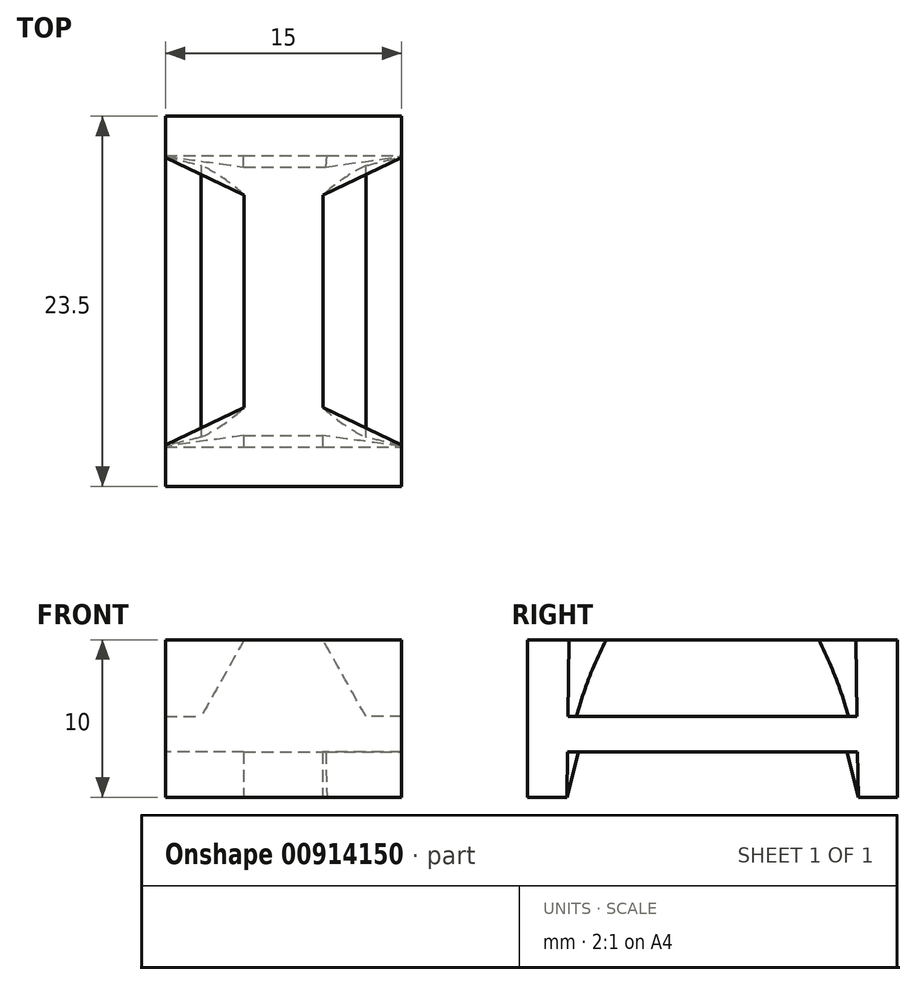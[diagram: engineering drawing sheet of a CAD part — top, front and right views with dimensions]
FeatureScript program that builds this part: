
annotation { "Feature Type Name" : "Feature", "Feature Type Description" : "" }
export const myFeature = defineFeature(function(context is Context, id is Id, definition is map)
    precondition{}
    {
        {
            var Q0;
            Q0=qCreatedBy(makeId("Top.planeOp"),FACE);
            var sketch = newSketch(context, id + "F0", { "sketchPlane" : qUnion([Q0])});
            skLineSegment(sketch, "E0.bottom", {"start": v(-7.5, 11.75) * mm, "end": v(7.5, 11.75) * mm});
            skLineSegment(sketch, "E0.top", {"start": v(-7.5, -11.75) * mm, "end": v(7.5, -11.75) * mm});
            skLineSegment(sketch, "E0.left", {"start": v(-7.5, 11.75) * mm, "end": v(-7.5, -11.75) * mm});
            skLineSegment(sketch, "E0.right", {"start": v(7.5, 11.75) * mm, "end": v(7.5, -11.75) * mm});
            skSolve(sketch);
        }
        {
            var Q0;
            Q0=makeQuery(id+"F0.imprint","IMPRINT",FACE,{"disambiguationData":[TD([[makeQuery(id+"F0.imprint","IMPRINT",EDGE,{"derivedFrom":sQuery(id+"F0.wireOp",EDGE,"E0.bottom")}),-1.0]])]});
            extrude(context, id + "F1", {"entities" : qUnion([Q0]), "depth" : 2.25 * mm, "offsetDistance" : 25 * mm, "symmetric" : true});
        }
        {
            var Q0;
            Q0=qCreatedBy(makeId("Top.planeOp"),FACE);
            cPlane(context, id + "F2", {"entities" : qUnion([Q0]), "cplaneType" : CPlaneType.OFFSET, "offset" : 6 * mm, "width" : 150 * mm, "height" : 150 * mm});
        }
        {
            var Q0;
            Q0=qCreatedBy(makeId("Top.planeOp"),FACE);
            cPlane(context, id + "F3", {"entities" : qUnion([Q0]), "cplaneType" : CPlaneType.OFFSET, "offset" : 4 * mm, "oppositeDirection" : true, "width" : 150 * mm, "height" : 150 * mm});
        }
        {
            var Q0;
            Q0=qCreatedBy(id+"F2.planeOp",FACE);
            var sketch = newSketch(context, id + "F4", { "sketchPlane" : qUnion([Q0])});
            skLineSegment(sketch, "E1", {"start": v(7.5, -11.75) * mm, "end": v(7.5, -9.12) * mm});
            skLineSegment(sketch, "E2", {"start": v(7.5, -9.12) * mm, "end": v(2.5, -6.75) * mm});
            skLineSegment(sketch, "E3", {"start": v(2.5, -6.75) * mm, "end": v(-2.5, -6.75) * mm});
            skLineSegment(sketch, "E4", {"start": v(-2.5, -6.75) * mm, "end": v(-7.5, -9.12) * mm});
            skLineSegment(sketch, "E5", {"start": v(-7.5, -9.12) * mm, "end": v(-7.5, -11.75) * mm});
            skLineSegment(sketch, "E6", {"start": v(-7.5, -11.75) * mm, "end": v(7.5, -11.75) * mm});
            skLineSegment(sketch, "E7.MirrorCS", {"start": v(-2.5, 6.75) * mm, "end": v(-7.5, 9.12) * mm});
            skLineSegment(sketch, "E8.MirrorCS", {"start": v(7.5, 11.75) * mm, "end": v(7.5, 9.12) * mm});
            skLineSegment(sketch, "E9.MirrorCS", {"start": v(7.5, 9.12) * mm, "end": v(2.5, 6.75) * mm});
            skLineSegment(sketch, "E10.MirrorCS", {"start": v(-7.5, 9.12) * mm, "end": v(-7.5, 11.75) * mm});
            skLineSegment(sketch, "E11.MirrorCS", {"start": v(2.5, 6.75) * mm, "end": v(-2.5, 6.75) * mm});
            skLineSegment(sketch, "E12.MirrorCS", {"start": v(-7.5, 11.75) * mm, "end": v(7.5, 11.75) * mm});
            skSolve(sketch);
        }
        {
            var Q0;
            Q0=qCreatedBy(id+"F3.planeOp",FACE);
            var sketch = newSketch(context, id + "F5", { "sketchPlane" : qUnion([Q0])});
            skLineSegment(sketch, "E13.bottom", {"start": v(-7.5, -11.75) * mm, "end": v(7.5, -11.75) * mm});
            skLineSegment(sketch, "E13.top", {"start": v(-7.5, -9.25) * mm, "end": v(-2.54, -9.25) * mm});
            skLineSegment(sketch, "E13.left", {"start": v(-7.5, -11.75) * mm, "end": v(-7.5, -9.25) * mm});
            skLineSegment(sketch, "E13.right", {"start": v(7.5, -11.75) * mm, "end": v(7.5, -9.25) * mm});
            skLineSegment(sketch, "E14.MirrorCS", {"start": v(7.5, 11.75) * mm, "end": v(7.5, 9.25) * mm});
            skLineSegment(sketch, "E15.MirrorCS", {"start": v(-7.5, 11.75) * mm, "end": v(-7.5, 9.25) * mm});
            skLineSegment(sketch, "E16.MirrorCS", {"start": v(-7.5, 9.25) * mm, "end": v(-2.54, 9.25) * mm});
            skLineSegment(sketch, "E17.MirrorCS", {"start": v(-7.5, 11.75) * mm, "end": v(7.5, 11.75) * mm});
            skLineSegment(sketch, "E18", {"start": v(-2.54, -9.25) * mm, "end": v(2.48, -9.25) * mm});
            skLineSegment(sketch, "E19", {"start": v(2.48, -9.25) * mm, "end": v(7.5, -9.25) * mm});
            skLineSegment(sketch, "E20", {"start": v(-2.54, 9.25) * mm, "end": v(2.76, 9.25) * mm});
            skLineSegment(sketch, "E21", {"start": v(2.76, 9.25) * mm, "end": v(7.5, 9.25) * mm});
            skSolve(sketch);
        }
        {
            var Q1;
            Q1=makeQuery(id+"F4.imprint","IMPRINT",FACE,{"disambiguationData":[TD([[makeQuery(id+"F4.imprint","IMPRINT",EDGE,{"derivedFrom":sQuery(id+"F4.wireOp",EDGE,"E7.MirrorCS")}),-1.0]])]});
            var Q2;
            Q2=makeQuery(id+"F5.imprint","IMPRINT",FACE,{"disambiguationData":[TD([[makeQuery(id+"F5.imprint","IMPRINT",EDGE,{"derivedFrom":sQuery(id+"F5.wireOp",EDGE,"E14.MirrorCS")}),-1.0]])]});
            loft(context, id + "F6", {"operationType" : NewBodyOperationType.ADD, "sheetProfilesArray" : [{ "sheetProfileEntities" : qUnion([Q1]) }, { "sheetProfileEntities" : qUnion([Q2]) }]});
        }
        {
            var Q1;
            Q1=makeQuery(id+"F4.imprint","IMPRINT",FACE,{"disambiguationData":[TD([[makeQuery(id+"F4.imprint","IMPRINT",EDGE,{"derivedFrom":sQuery(id+"F4.wireOp",EDGE,"E1")}),1.0]])]});
            var Q2;
            Q2=makeQuery(id+"F5.imprint","IMPRINT",FACE,{"disambiguationData":[TD([[makeQuery(id+"F5.imprint","IMPRINT",EDGE,{"derivedFrom":sQuery(id+"F5.wireOp",EDGE,"E13.bottom")}),1.0]])]});
            loft(context, id + "F7", {"operationType" : NewBodyOperationType.ADD, "sheetProfilesArray" : [{ "sheetProfileEntities" : qUnion([Q1]) }, { "sheetProfileEntities" : qUnion([Q2]) }]});
        }
        {
            var Q0;
            Q0=qCreatedBy(makeId("Front.planeOp"),FACE);
            cPlane(context, id + "F8", {"entities" : qUnion([Q0]), "cplaneType" : CPlaneType.OFFSET, "offset" : 10.1 * mm, "width" : 150 * mm, "height" : 150 * mm});
        }
        {
            var Q0;
            Q0=qCreatedBy(id+"F8.planeOp",FACE);
            var sketch = newSketch(context, id + "F9", { "sketchPlane" : qUnion([Q0])});
            skLineSegment(sketch, "E22", {"start": v(5.86, 0) * mm, "end": v(2.5, 6) * mm});
            skLineSegment(sketch, "E23", {"start": v(2.5, 6) * mm, "end": v(-2.5, 6) * mm});
            skLineSegment(sketch, "E24", {"start": v(-2.5, 6) * mm, "end": v(-5.86, 0) * mm});
            skLineSegment(sketch, "E25", {"start": v(-5.86, 0) * mm, "end": v(5.86, 0) * mm});
            skSolve(sketch);
        }
        {
            var Q0;
            Q0=makeQuery(id+"F9.imprint","IMPRINT",FACE,{"disambiguationData":[TD([[makeQuery(id+"F9.imprint","IMPRINT",EDGE,{"derivedFrom":sQuery(id+"F9.wireOp",EDGE,"E22")}),1.0]])]});
            extrude(context, id + "F10", {"entities" : qUnion([Q0]), "operationType" : NewBodyOperationType.ADD, "oppositeDirection" : true, "depth" : 20.1 * mm, "offsetDistance" : 25 * mm});
        }
    });
